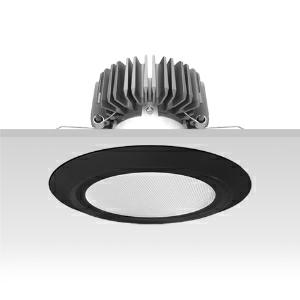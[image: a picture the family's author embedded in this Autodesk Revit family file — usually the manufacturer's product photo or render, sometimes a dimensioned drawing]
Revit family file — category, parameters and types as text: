
# Revit family: 3f_filippi_-_3f_reno_bianco_ampio_3f_filippi_-_30691_a01038_-_3f_reno_200_wh_4000-930_dali_wide___vs_bk_c76b
name_source: partatom
category: Lighting Fixtures
units: mm (PartAtom-declared; Revit-internal decimal feet)

## family parameters
Cut with Voids When Loaded = No
Host = Face
Light Source = No
Part Type = Normal
Room Calculation Point = No
Round Connector Dimension = Use Diameter
Shared = No

## types (1)
- 3F Filippi - 3F Reno Bianco Ampio (1 x LED, 2801 lm, 43 W, 3000 K)
    Apparent Load = 43 VA
    Approval mark = CE
    CIE Flux Codes = 75 94 99 100 100
    Color Rendering = 90
    Color Temperature = 3000 K
    Control Gear = Electronic transformer
    Default Elevation = 1800 mm
    Description = ILLUMINOTECHNICAL
Luminous efficiency 100% (DLOR 100%, ULOR 0%).
Initial luminous flux of the luminaire 2801 lm.
Direct symmetric wide distribution.
Installation Interdistance Transv.D = 1.16 x hu - Long.D = 1.14 x hu.
Tabular UGR (CIE 117 - 4H-8H; S=0.25H; 70/50/20): RUG 22.1 - 22.
Beam angle: 74° - 74°.
Luminous efficacy 65 lm/W.
Lifetime (L90/B10): 30000 h. (tq+25°C)
Lifetime (L85/B10): 50000 h. (tq+25°C)
Lifetime (L70/B10): 80000 h. (tq+25°C)
Sudden decreased luminous flux after 50000 hours: 0% (C0).
Photobiological safety in compliance with IEC/TR 62778: RG1 low risk, (IEC 62471).
In compliance with IEC/EN 62722-2-1 - IEC/EN 62717 standards.

SOURCE
Compact LED module 4000/930.
Energy efficiency class (UE 2019/2020 - UE 2019/2015): F.
CIE 13.3 Colour rendering index: CRI >90 (R9 >50%).
IES TM-30 Fidelity Index: Rf = 92 Rg = 101.
CCT nominal colour temperature 3000 K.
Colour initial tolerance (MacAdam): SDCM 3.
Zhaga Book 3 compliant.

MECHANICAL
Passive heat dissipator in die-casting aluminium, oversized, for optimum thermal management of the LED module.
Parabolic element with graduated/concentric rings in white polycarbonate.
Transparent external lens with glossy and satin differentiated surfaces, with a cooling and anti-insect system in methacrylate (PMMA).
Fastening spring clips in stainless steel.
Dimensions: diameter 226 mm, height 146 mm. Weight 1.855 kg.
IP44 protection degree for exposed part, IP20 for recessed part.
Mechanical strength to impacts IK06 (1 joule).
Glow-wire test resistance 650°C.

ELECTRICAL
Wiring on a separate unit.
Halogen Free DALI-2 DATI (Parts 251, 252, 253), PUSH-DIM, electronic wiring 230V-50/60Hz, power factor 0.97 at full load, THD <25%, constant output current, SELV, class II, 1 driver, 1 DALI addresse.
Power of the luminaire 43 W.
ENEC - CE.
SAFE FLICKER: PstLM=<1 and SVM=<0.4 (IEC TR 61547-1 and IEC TR 63158), to ensure a more comfortable and safe light.
Luminaire compliant with EN 60598-2-22 for power supply from a centralised emergency system CPSS (Central Power Supply System), not incorporated in the luminaire - high risk areas excluded. The default power and flux are 100% in AC and 100% in DC.
Ambient temperature from 0°C to +25°C.
Temperature class T6 max 85°C.
Relative humidity UR: <85%.

INSTALLATION
Pull-up recessed fitting.
False ceiling carving: 200 mm.
All accessories dedicated to this product are available on the Catalog and on our website www.3F-Filippi.com.

ACCESSORIES
A01038 - Anti-glare microprismatic VS moulded glass, tempered, not flammable, locked and in line with the trim, in black polycarbonate.

APPLICATIONS
Environments: architectural, commercial, exhibition areas, transit areas, corridors, shops, display windows, service areas.
In false ceilings with narrow voids.

LIGHT MANAGEMENT
Recommended minimum setting: 10%.
The luminaire, equipped with (DALI-2 DATI) driver, can be controlled manually with 3F Easy Dim technology or automatically/manually with wired or wireless DALI/D2D control systems.
The D2D driver guarantees interoperability with other devices with the same certification by making the following information available:
Device Data (Part 251), Energy Report (Part 252), Diagnosis & Maintenance (Part 253).
In electrical systems without a regulation system (manual or automatic) and DALI bus, a suitable jumper must be made on the DA-DA terminals of the appliance.

WARNING
Luminaire designed for disposal/recycling at end-of-life.
Replaceable (LED only) light source by a professional. Replaceable control gear by a professional.
    Height = 0 mm  [stored 0 ft]
    Lamp = 1 x LED
    Lamp Light Flux = 2801 lm
    Lamp Power = 43 W
    Lamp count = 1
    Length = 226 mm
    Lifetime = 50000 h
    Luminous efficacy = 65 lm/W
    Manufacturer = 3F Filippi
    ModVariant = No
    Model = 3F Filippi - 30691+A01038 - 3F Reno 200 WH 4000-930 DALI WIDE + VS BK
    Mounting Place = Ceiling
    Mounting Type = Recessed
    Number of Poles = 1
    OnlyDefault = Yes
    Power Factor = 1
    Product Name = 3F Filippi - 3F Reno Bianco Ampio
    Product group = recessed luminaire
    ProductGroupID = 4
    Protection Class = Protection class II
    Protection Degree = IP 20
    RLX_Detail_Level = 1
    RLX_Emergency_Light_Flux = 0 lm
    RLX_Emergency_Type = 0
    RLX_Emergency_Type_DB = No
    RlxData = <blob elided: 99037 chars, md5=7766787a>
    Socket = socket
    Standby Power = 0 W
    System Light Flux = 2801 lm
    System Power = 43 W
    Type Comments = Product without accessories
    Type Image = 3ffilippi_3f_reno_200_bk_vs_smp.jpg
    URL = http://relux.com
    VarID = ---
    Voltage = 0 V
    Weight = 0.00 kg
    Width = 0 mm  [stored 0 ft]

note: [stored X ft] marks values corroborated as IEEE doubles in the binary element streams (Revit-internal decimal feet)

## geometry (parser evidence)
native form markers: Blend x4, Sweep x9
no freeform markers — native parametric forms only
